# Revit family: Стальной фонарный столб Ретро 3 мод.17 Арт 9940
name_source: partatom
category: Антураж
revit_build: Autodesk Revit 2018 (Build: 20180423_1000(x64)
units: mm (PartAtom-declared; Revit-internal decimal feet)

## family parameters
Всегда вертикально = Да
Источник визуального образа = Геометрия семейства
На основе рабочей плоскости = Нет
Общий = Нет
При загрузке вырезать с полостями = Нет
Точка расчета площади = Нет

## types (6) — shared parameters
URL = https://hobbyka.ru
Артикул товара = Арт. 9940
Группа модели = Светильники со стальными опорами
Длина = 1405 мм
Изготовитель = ООО «Хоббика»
Изображение типоразмера = Стальной фонарный столб Ретро 3 мод.17 Арт 9940.jpg
Материал изделия = Сталь
Цвет каркаса = Сталь
Ширина = 368 мм

## per-type parameters (varying)
| type | Версия 3,89 м | Версия 4,39 м | Версия 4,89 м | Версия 5,39 м | Версия 5,89 м | Высота | Высота опоры | Описание |
| Версия 3,89 м | Да | Нет | Нет | Нет | Нет | 3890 мм | 2493 мм | Стальной фонарный столб Ретро 3 мод.17. Версия 3,89 м |
| Версия 4,39 м | Нет | Да | Нет | Нет | Нет | 4390 мм | 2993 мм | Стальной фонарный столб Ретро 3 мод.17. Версия 4,39 м |
| Версия 4,89 м | Нет | Нет | Да | Нет | Нет | 4890 мм | 3493 мм | Стальной фонарный столб Ретро 3 мод.17. Версия 4,89 м |
| Версия 5,39 м | Нет | Нет | Нет | Да | Нет | 5390 мм | 3993 мм | Стальной фонарный столб Ретро 3 мод.17. Версия 5,39 м |
| Версия 5,89 м | Нет | Нет | Нет | Нет | Да | 5890 мм | 4493 мм | Стальной фонарный столб Ретро 3 мод.17. Версия 5,89 м |
| Версия 6,39 м | Нет | Нет | Нет | Нет | Нет | 6390 мм | 4993 мм | Стальной фонарный столб Ретро 3 мод.17. Версия 6,39 м |
